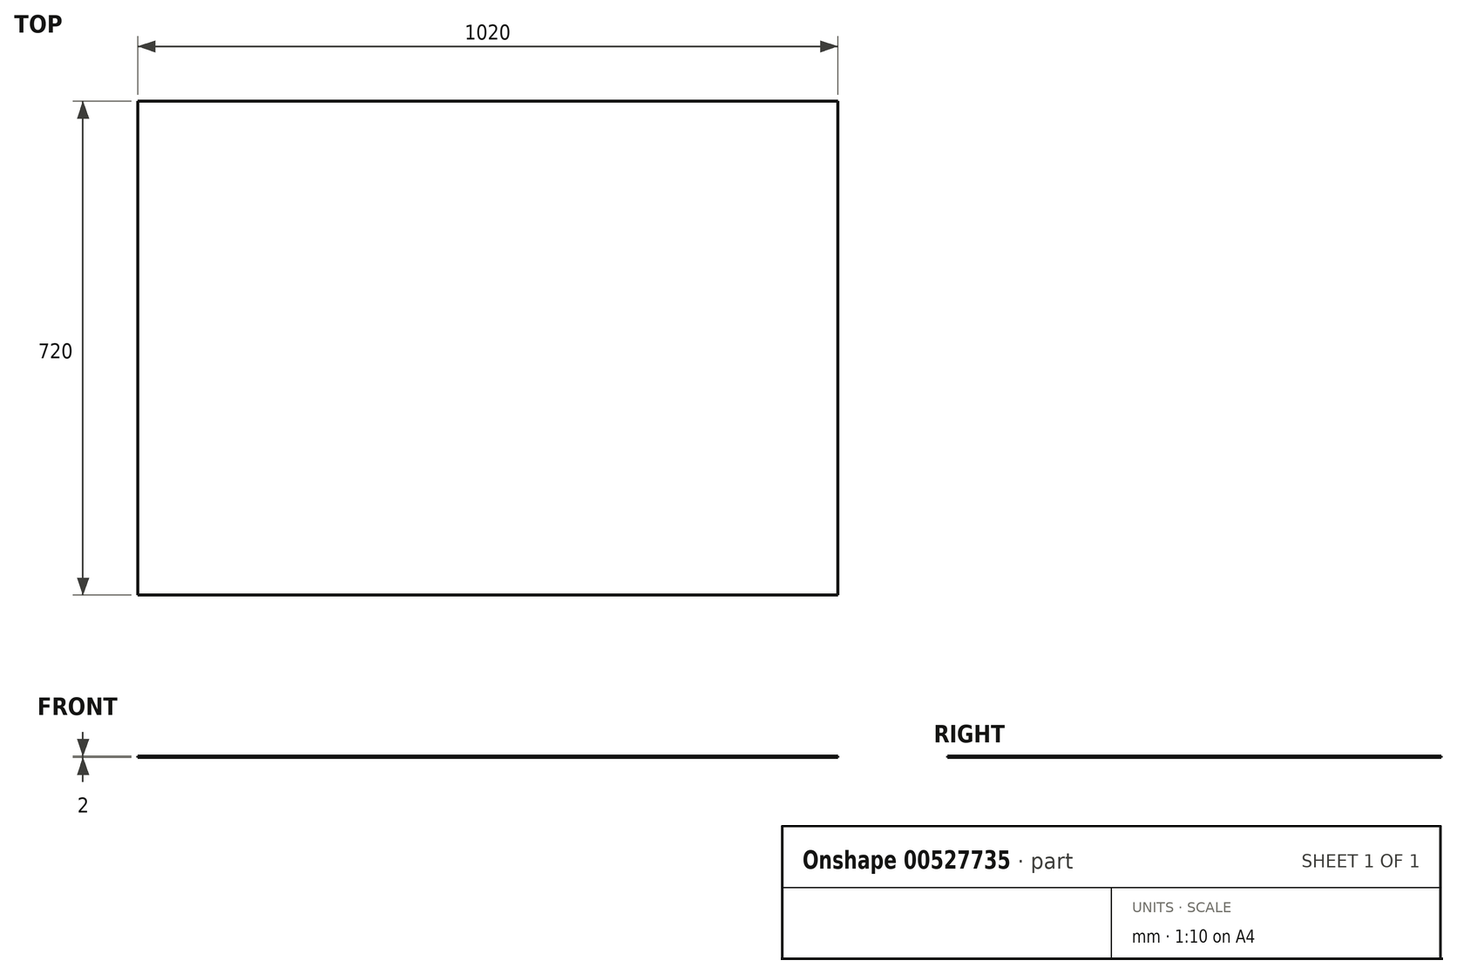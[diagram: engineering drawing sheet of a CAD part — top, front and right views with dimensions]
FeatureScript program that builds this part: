
annotation { "Feature Type Name" : "Feature", "Feature Type Description" : "" }
export const myFeature = defineFeature(function(context is Context, id is Id, definition is map)
    precondition{}
    {
        {
            var Q0;
            Q0=qCreatedBy(makeId("Top.planeOp"),FACE);
            var sketch = newSketch(context, id + "F0", { "sketchPlane" : qUnion([Q0])});
            skLineSegment(sketch, "E0.bottom", {"start": v(0, 0) * mm, "end": v(-1020, 0) * mm});
            skLineSegment(sketch, "E0.top", {"start": v(0, -720) * mm, "end": v(-1020, -720) * mm});
            skLineSegment(sketch, "E0.left", {"start": v(0, 0) * mm, "end": v(0, -720) * mm});
            skLineSegment(sketch, "E0.right", {"start": v(-1020, 0) * mm, "end": v(-1020, -720) * mm});
            skSolve(sketch);
        }
        {
            var Q0;
            Q0 = qSketchRegion(id + "F0", true);
            extrude(context, id + "F1", {"entities" : qUnion([Q0]), "depth" : 2 * mm, "offsetDistance" : 25 * mm});
        }
    });
